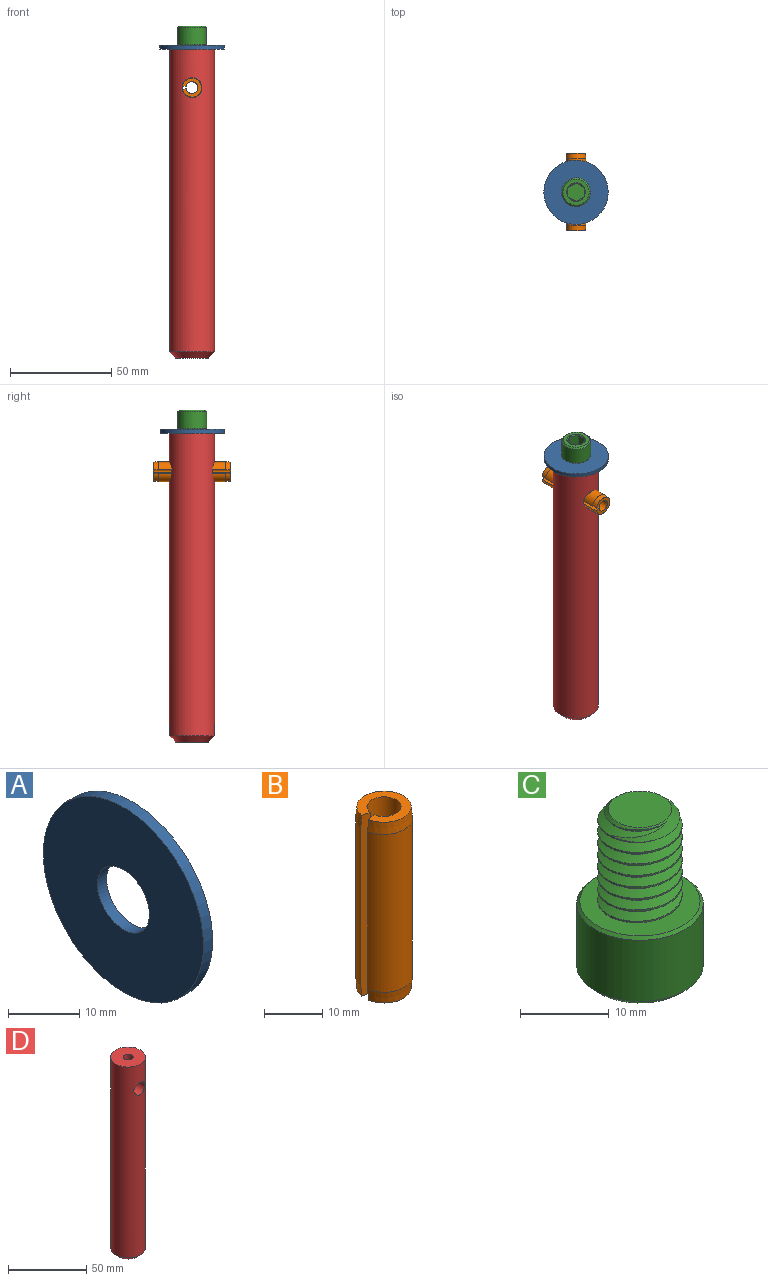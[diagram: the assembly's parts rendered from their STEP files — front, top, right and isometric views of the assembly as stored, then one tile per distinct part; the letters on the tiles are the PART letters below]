
ASSEMBLY  parts=4 mates=3
PART A: 4 faces, bbox 1.8x31.8x31.8 mm
  f0: plane 31.75x31.75mm, normal (1,0,0), area 708.2mm2, adj f2,f3
  f1: plane 31.75x31.75mm, normal (-1,0,0), area 708.2mm2, adj f2,f3
  f2: cylinder r=15.88mm len=31.75mm, axis (-1,0,0), area 182.4mm2, adj f0,f1
  f3: cylinder r=5.16mm len=10.31mm, axis (-1,0,0), area 59.2mm2, adj f0,f1
PART B: 8 faces, bbox 9.7x9.8x38.1 mm
  f0: cylinder r=2.93mm len=38.1mm, axis (0,0,-1), area 663.3mm2, adj f1,f3,f4,f5
  f1: plane 38.1x1.93mm, normal (-0.17,0.98,0), area 74mm2, adj f0,f2,f4,f5,f6,f7
  f2: cylinder r=4.89mm len=33.27mm, axis (0,0,-1), area 965.4mm2, adj f1,f3,f6,f7
  f3: plane 38.1x1.93mm, normal (-0.17,-0.98,0), area 74mm2, adj f0,f2,f4,f5,f6,f7
  f4: plane 9.35x9.28mm, normal (0,0,1), area 39.3mm2, adj f0,f1,f3,f7
  f5: plane 9.35x9.28mm, normal (0,0,-1), area 39.3mm2, adj f0,f1,f3,f6
  f6: cone r=4.89mm half-angle=5.1deg, axis (0,0,1), area 68.7mm2, adj f1,f2,f3,f5
  f7: cone r=4.67mm half-angle=5.1deg, axis (0,0,-1), area 68.7mm2, adj f1,f2,f3,f4
PART C: 24 faces, bbox 16x16x24.6 mm
  f0: cylinder r=4.76mm len=11.51mm, axis (0,0,1), area 8mm2, adj f2,f4,f5,f6
  f1: plane 7.14x7.14mm, normal (0,0,1), area 40.1mm2, adj f2
  f2: cone r=3.57mm half-angle=45deg, axis (0,0,-1), area 24.1mm2, adj f0,f1,f3,f4,f5
  f3: cylinder r=3.73mm len=12.54mm, axis (0,0,-1), area 48.7mm2, adj f2,f4,f5,f6
  f4: bspline ~13.56x11mm, area 240.9mm2, adj f0,f2,f3,f6
  f5: bspline ~14.09x11mm, area 238.5mm2, adj f0,f2,f3,f6
  f6: plane 14.2x14.2mm, normal (0,0,1), area 87.6mm2, adj f0,f3,f4,f5,f23
  f7: cylinder r=7.14mm len=14.29mm, axis (0,0,1), area 379.4mm2, adj f22,f23
  f8: plane 12.86x12.86mm, normal (0,0,-1), area 63.9mm2, adj f9,f10,f11,f12,f13,f14,f22
  f9: cone r=4.58mm half-angle=45deg, axis (0,0,-1), area 0mm2, adj f8,f16
  f10: cone r=4.58mm half-angle=45deg, axis (0,0,-1), area 0mm2, adj f8,f17
  f11: cone r=4.58mm half-angle=45deg, axis (0,0,-1), area 0mm2, adj f8,f18
  f12: cone r=4.58mm half-angle=45deg, axis (0,0,-1), area 0mm2, adj f8,f19
  f13: cone r=4.58mm half-angle=45deg, axis (0,0,-1), area 0mm2, adj f8,f20
  f14: cone r=4.58mm half-angle=45deg, axis (0,0,-1), area 0mm2, adj f8,f21
  f15: plane 9.17x7.94mm, normal (0,0,-1), area 54.6mm2, adj f16,f17,f18,f19,f20,f21
  f16: plane 7.69x5.71mm, normal (-0.5,-0.87,0), area 25.4mm2, adj f9,f15,f17,f21
  f17: plane 7.69x6.33mm, normal (-1,0,0), area 25.4mm2, adj f10,f15,f16,f18
  f18: plane 7.69x5.71mm, normal (-0.5,0.87,0), area 25.4mm2, adj f11,f15,f17,f19
  f19: plane 7.69x5.71mm, normal (0.5,0.87,0), area 25.4mm2, adj f12,f15,f18,f20
  f20: plane 7.69x6.33mm, normal (1,0,0), area 25.4mm2, adj f13,f15,f19,f21
  f21: plane 7.69x5.71mm, normal (0.5,-0.87,0), area 25.4mm2, adj f14,f15,f16,f20
  f22: cone r=6.43mm half-angle=45deg, axis (0,0,1), area 43.1mm2, adj f7,f8
  f23: cone r=7.14mm half-angle=45deg, axis (0,0,-1), area 22.1mm2, adj f6,f7
PART D: 7 faces, bbox 22.2x22.2x152.4 mm
  f0: cylinder r=11.11mm len=149.23mm, axis (0,0,-1), area 10273.3mm2, adj f1,f3,f4
  f1: plane 22.23x22.23mm, normal (0,0,1), area 356.3mm2, adj f0,f5
  f2: plane 15.88x15.88mm, normal (0,0,-1), area 197.9mm2, adj f3
  f3: cone r=11.11mm half-angle=45deg, axis (0,0,1), area 268.7mm2, adj f0,f2
  f4: cylinder r=4.76mm len=22.23mm, axis (0,-1,0), area 633.4mm2, adj f0
  f5: cylinder r=3.17mm len=12.7mm, axis (0,0,1), area 253.4mm2, adj f1,f6
  f6: plane 6.35x6.35mm, normal (0,0,1), area 31.7mm2, adj f5
PLACE A rot(axis=(0.71,0,0.71),180deg) t=(-11.58,10.25,89.15)mm
PLACE B rot(axis=(-1,0,0),90deg) t=(-11.58,10.42,70.1)mm
PLACE C rot(axis=(1,0,0),180deg) t=(-11.58,10.25,78.28)mm
PLACE D t=(-11.58,10.25,-63.25)mm
MATE fastened C.f0 <-> A.f2  axis (0,0,-1) through (-11.58,10.25,90.98)mm
MATE fastened B.f0 <-> D.f4  axis (0,-1,0) through (-11.58,10.42,70.1)mm
MATE fastened A.f2 <-> D.f5  axis (0,0,-1) through (-11.58,10.25,89.15)mm
